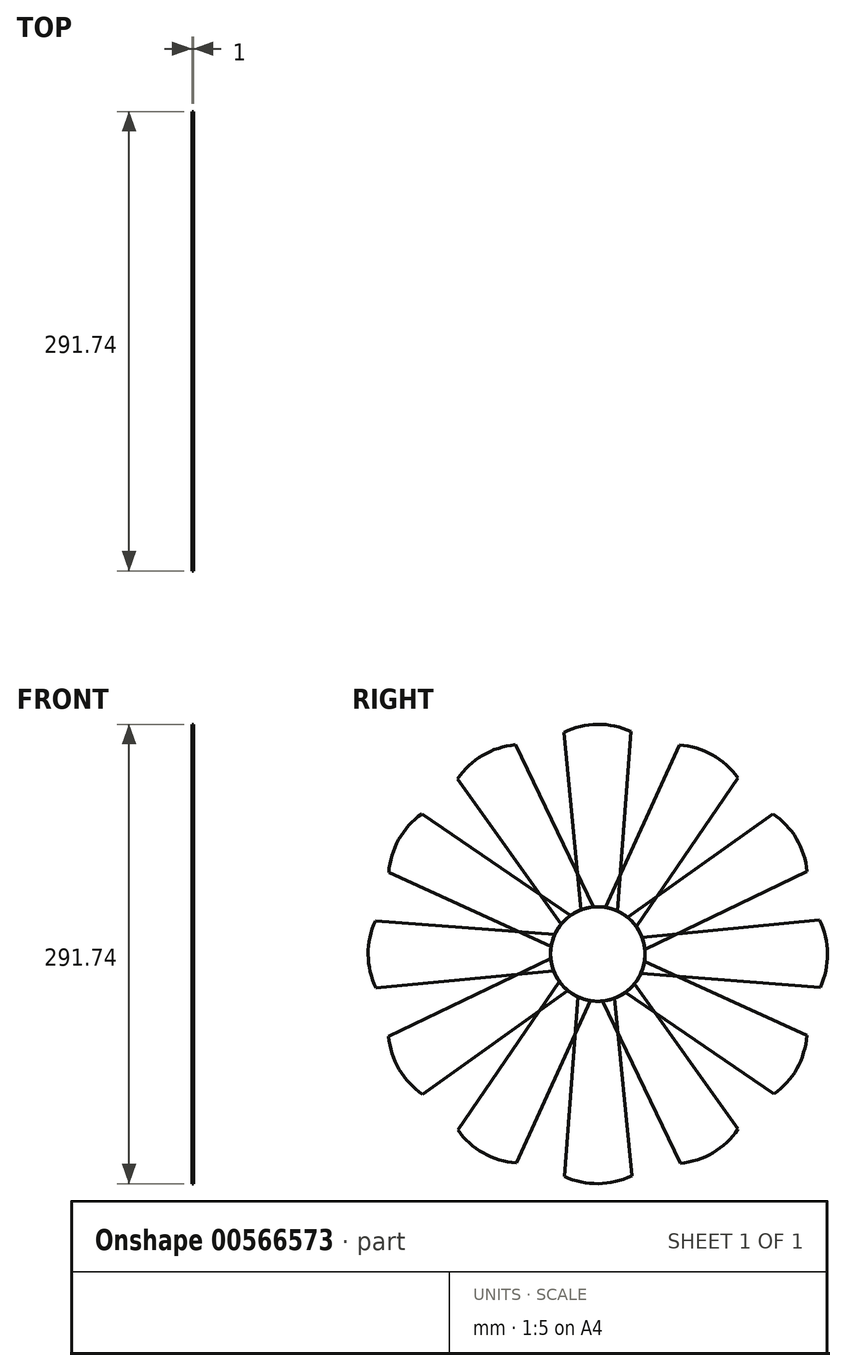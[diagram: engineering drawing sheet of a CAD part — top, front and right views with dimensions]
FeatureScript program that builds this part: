
annotation { "Feature Type Name" : "Feature", "Feature Type Description" : "" }
export const myFeature = defineFeature(function(context is Context, id is Id, definition is map)
    precondition{}
    {
        {
            var Q0;
            Q0=qCreatedBy(makeId("Right.planeOp"),FACE);
            var sketch = newSketch(context, id + "F0", { "sketchPlane" : qUnion([Q0])});
            skCircle(sketch, "E0", {"center": v(0, 0) * mm, "radius": 30 * mm});
            skLineSegment(sketch, "E1", {"start": v(0, 30) * mm, "end": v(0, -30) * mm, "construction": true});
            skLineSegment(sketch, "E2", {"start": v(0, -30) * mm, "end": v(-30, 0) * mm, "construction": true});
            skLineSegment(sketch, "E3", {"start": v(-30, 0) * mm, "end": v(30, 0) * mm, "construction": true});
            skLineSegment(sketch, "E4", {"start": v(30, 0) * mm, "end": v(-1.34, 29.97) * mm, "construction": true});
            skLineSegment(sketch, "E5", {"start": v(-1.34, 29.97) * mm, "end": v(-30, 0) * mm, "construction": true});
            skLineSegment(sketch, "E6", {"start": v(30, 0) * mm, "end": v(0, -30) * mm, "construction": true});
            skLineSegment(sketch, "E7", {"start": v(14.33, 14.98) * mm, "end": v(-15.67, 14.98) * mm, "construction": true});
            skLineSegment(sketch, "E8", {"start": v(-15.67, 14.98) * mm, "end": v(-15.67, -14.33) * mm, "construction": true});
            skLineSegment(sketch, "E9", {"start": v(-15.67, -14.33) * mm, "end": v(15.67, -14.33) * mm, "construction": true});
            skLineSegment(sketch, "E10", {"start": v(14.33, 14.98) * mm, "end": v(14.33, -14.33) * mm, "construction": true});
            skLineSegment(sketch, "E11", {"start": v(-15.67, 14.98) * mm, "end": v(20.87, -21.55) * mm, "construction": true});
            skLineSegment(sketch, "E12", {"start": v(20.87, -21.55) * mm, "end": v(-21.55, 20.87) * mm, "construction": true});
            skLineSegment(sketch, "E13", {"start": v(14.33, 14.98) * mm, "end": v(-22.75, -19.56) * mm, "construction": true});
            skLineSegment(sketch, "E14", {"start": v(-22.75, -19.56) * mm, "end": v(21.12, 21.3) * mm, "construction": true});
            skLineSegment(sketch, "E15", {"start": v(9.44, 10.43) * mm, "end": v(-7.07, 23.98) * mm, "construction": true});
            skLineSegment(sketch, "E16", {"start": v(21.12, 21.3) * mm, "end": v(21.12, 141.3) * mm, "construction": true});
            skLineSegment(sketch, "E17", {"start": v(-21.55, 20.87) * mm, "end": v(-21.55, 140.87) * mm, "construction": true});
            skLineSegment(sketch, "E18", {"start": v(12.46, 27.3) * mm, "end": v(21.12, 141.3) * mm});
            skLineSegment(sketch, "E19", {"start": v(-10.67, 28.04) * mm, "end": v(-21.55, 140.87) * mm});
            skArc(sketch, "E20", {"start": v(21.12, 141.3) * mm, "mid": v(-0.27, 145.87) * mm, "end": v(-21.55, 140.87) * mm});
            skSolve(sketch);
        }
        {
            var Q0;
            Q0 = qSketchRegion(id + "F0", true);
            extrude(context, id + "F1", {"entities" : qUnion([Q0]), "oppositeDirection" : true, "depth" : 1 * mm, "offsetDistance" : 25 * mm});
        }
        {
            var Q0;
            Q0=makeQuery(id+"F1.opExtrude","CAP_FACE",FACE,{"disambiguationData":[OSD([sQuery(id+"F0.wireOp",EDGE,"E0"),sQuery(id+"F0.wireOp",EDGE,"E18"),sQuery(id+"F0.wireOp",EDGE,"E19"),sQuery(id+"F0.wireOp",EDGE,"E20")])],"isStart":false});
            var sketch = newSketch(context, id + "F2", { "sketchPlane" : qUnion([Q0])});
            skCircle(sketch, "E21", {"center": v(0, 0) * mm, "radius": 30 * mm});
            skSolve(sketch);
        }
        {
            var Q0;
            Q0=makeQuery(id+"F1.opExtrude","SWEPT_BODY",BODY,{"disambiguationData":[OSD([sQuery(id+"F0.wireOp",EDGE,"E0"),sQuery(id+"F0.wireOp",EDGE,"E18"),sQuery(id+"F0.wireOp",EDGE,"E19"),sQuery(id+"F0.wireOp",EDGE,"E20")])]});
            var Q1;
            Q1=sQuery(id+"F2.wireOp",EDGE,"E21");
            circularPattern(context, id + "F3", {"entities" : qUnion([Q0]), "axis" : qUnion([Q1]), "angle" : 360 * degree, "instanceCount" : 12, "equalSpace" : true});
        }
    });
